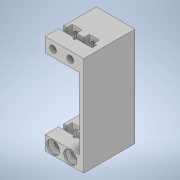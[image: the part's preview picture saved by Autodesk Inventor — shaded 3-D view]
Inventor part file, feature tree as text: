
AUTODESK INVENTOR PART (.ipt)
format: ipt  version: 2020 (Build 240168000, 168)  size: 201,728 bytes
history: native  units: mm
features: other x3, projected_geometry x2, extrude x1, sketch x1
ambient origin geometry x8: Origin, YZ Plane, XZ Plane, XY Plane, X Axis, Y Axis, Z Axis, Center Point
bodies: Solide2 (feature_tree)
feature tree (7):
  other  "servo_holder.ipt"
  extrude  "Extrusion6"  Depth=10.0mm
  other  "Solide1::servo_holder.ipt"
  other  "FonctionRepérage2"
  sketch  "Esquisse7"
  projected_geometry  "Boucle projetée2"
  projected_geometry  "Boucle projetée3"
